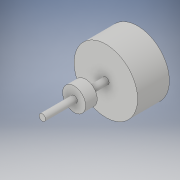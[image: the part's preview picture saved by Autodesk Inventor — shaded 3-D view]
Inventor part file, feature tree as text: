
AUTODESK INVENTOR PART (.ipt)
format: ipt  version: 2018.2 (Build 222227000, 227)  size: 111,616 bytes
history: native  units: in
note: dims shown in document units (in); Inventor stores cm internally (conversion verified against a paired STEP export)
features: extrude x4, sketch x4
ambient origin geometry x8: Origin, YZ Plane, XZ Plane, XY Plane, X Axis, Y Axis, Z Axis, Center Point
bodies: Solid1 (feature_tree)
feature tree (8):
  extrude  "Extrusion1"  Depth=0.8661in TaperAngle=0.0deg
  extrude  "Extrusion2"  Depth=0.5512in TaperAngle=0.0deg
  extrude  "Extrusion3"  Depth=0.315in TaperAngle=0.0deg
  extrude  "Extrusion4"  [1 undecoded]
  sketch  "Sketch1"  dims[d0=1.7323in d1=0.8661in d2=0.0in]
  sketch  "Sketch2"  dims[d3=0.1772in d4=0.5512in d5=0.0in]
  sketch  "Sketch3"  dims[d6=0.6299in d7=0.315in d8=0.0in]
  sketch  "Sketch4"  dims[d9=0.8661in d10=0.0in]
note: 1 required parameter value undecoded (feature->parameter linkage not recoverable at this tier; creation-order binding heuristic only, values carry confidence <= 0.55)
